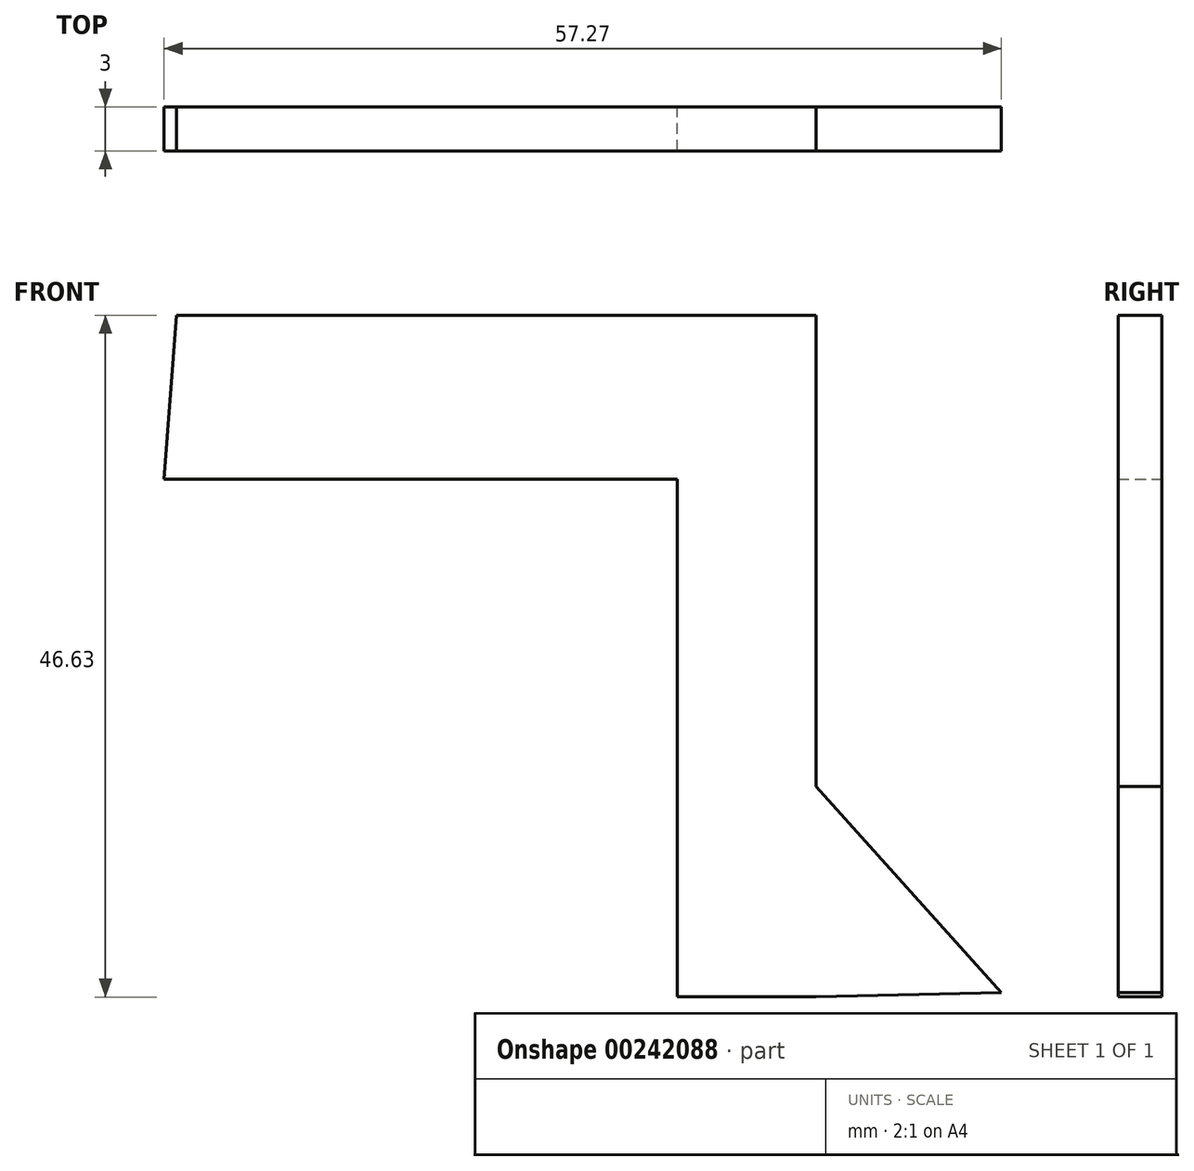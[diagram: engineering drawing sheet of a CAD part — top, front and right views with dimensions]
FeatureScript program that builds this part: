
annotation { "Feature Type Name" : "Feature", "Feature Type Description" : "" }
export const myFeature = defineFeature(function(context is Context, id is Id, definition is map)
    precondition{}
    {
        {
            var Q0;
            Q0=qCreatedBy(makeId("Front.planeOp"),FACE);
            var sketch = newSketch(context, id + "F0", { "sketchPlane" : qUnion([Q0])});
            skLineSegment(sketch, "E0", {"start": v(-29.07, 27.63) * mm, "end": v(14.68, 27.63) * mm});
            skLineSegment(sketch, "E1", {"start": v(14.68, -19) * mm, "end": v(5.18, -19) * mm});
            skLineSegment(sketch, "E2", {"start": v(5.18, -19) * mm, "end": v(5.18, 16.4) * mm});
            skLineSegment(sketch, "E3", {"start": v(5.18, 16.4) * mm, "end": v(-29.93, 16.4) * mm});
            skLineSegment(sketch, "E4", {"start": v(-29.93, 16.4) * mm, "end": v(-29.07, 27.63) * mm});
            skLineSegment(sketch, "E5", {"start": v(14.68, -4.6) * mm, "end": v(27.34, -18.7) * mm});
            skLineSegment(sketch, "E6", {"start": v(27.34, -18.7) * mm, "end": v(14.68, -19) * mm});
            skLineSegment(sketch, "E7", {"start": v(14.68, -4.6) * mm, "end": v(14.68, 27.63) * mm});
            skSolve(sketch);
        }
        {
            var Q0;
            Q0 = qSketchRegion(id + "F0", true);
            extrude(context, id + "F1", {"entities" : qUnion([Q0]), "depth" : 3 * mm});
        }
    });
